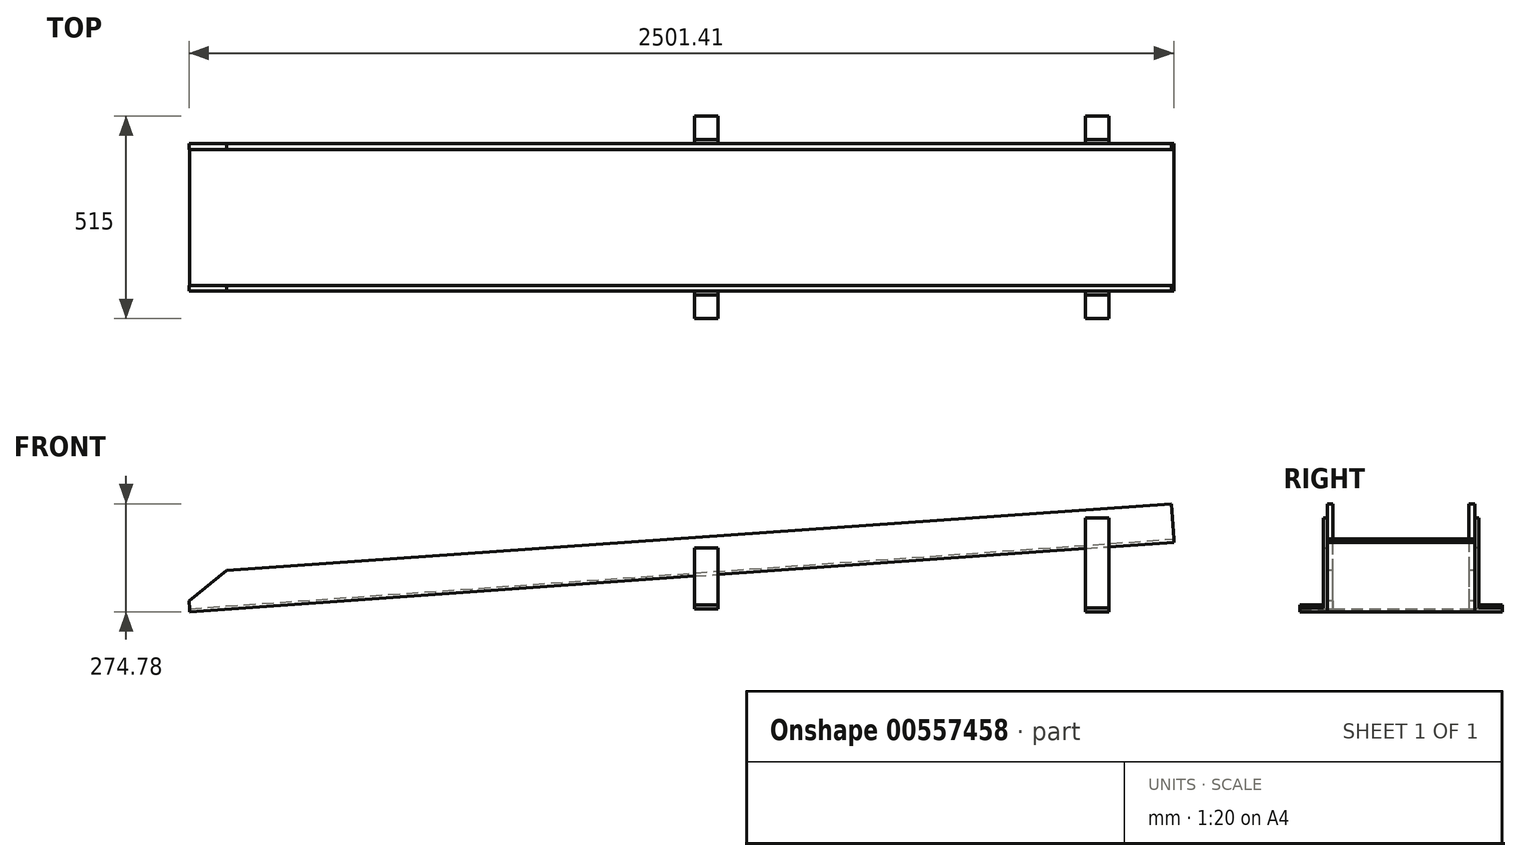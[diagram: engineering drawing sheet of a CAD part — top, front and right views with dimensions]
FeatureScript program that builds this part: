
annotation { "Feature Type Name" : "Feature", "Feature Type Description" : "" }
export const myFeature = defineFeature(function(context is Context, id is Id, definition is map)
    precondition{}
    {
        {
            var Q0;
            Q0=qCreatedBy(makeId("Front.planeOp"),FACE);
            var sketch = newSketch(context, id + "F0", { "sketchPlane" : qUnion([Q0])});
            skLineSegment(sketch, "E0", {"start": v(-1084.35, 0) * mm, "end": v(1415.65, 176.98) * mm});
            skLineSegment(sketch, "E1", {"start": v(1415.65, 176.98) * mm, "end": v(1415.65, 0) * mm});
            skLineSegment(sketch, "E2", {"start": v(1415.65, 0) * mm, "end": v(-1084.35, 0) * mm});
            skLineSegment(sketch, "E3", {"start": v(1415.65, 185) * mm, "end": v(-1084.35, 8.02) * mm});
            skLineSegment(sketch, "E4", {"start": v(-1084.35, 8.02) * mm, "end": v(-1084.35, 0) * mm});
            skLineSegment(sketch, "E5", {"start": v(1415.65, 176.98) * mm, "end": v(1415.65, 185) * mm});
            skSolve(sketch);
        }
        {
            var Q0;
            Q0=makeQuery(id+"F0.imprint","IMPRINT",FACE,{"disambiguationData":[TD([[makeQuery(id+"F0.imprint","IMPRINT",EDGE,{"derivedFrom":sQuery(id+"F0.wireOp",EDGE,"E0")}),1.0]])]});
            extrude(context, id + "F1", {"entities" : qUnion([Q0]), "endBound" : BoundingType.SYMMETRIC, "depth" : 375 * mm, "offsetDistance" : 25 * mm});
        }
        {
            var Q0;
            Q0=makeQuery(id+"F1.opExtrude","SWEPT_FACE",FACE,{"disambiguationData":[OSD([sQuery(id+"F0.wireOp",EDGE,"E3")])]});
            var sketch = newSketch(context, id + "F2", { "sketchPlane" : qUnion([Q0])});
            skLineSegment(sketch, "E6", {"start": v(1425.18, -187.5) * mm, "end": v(-1081.07, -187.5) * mm});
            skLineSegment(sketch, "E7", {"start": v(-1081.07, -187.5) * mm, "end": v(-1081.07, -172.5) * mm});
            skLineSegment(sketch, "E8", {"start": v(-1081.07, -172.5) * mm, "end": v(1425.18, -172.5) * mm});
            skLineSegment(sketch, "E9", {"start": v(1425.18, -172.5) * mm, "end": v(1425.18, -187.5) * mm});
            skLineSegment(sketch, "E10", {"start": v(1425.18, 187.5) * mm, "end": v(1425.18, 172.5) * mm});
            skLineSegment(sketch, "E11", {"start": v(1425.18, 172.5) * mm, "end": v(-1081.07, 172.5) * mm});
            skLineSegment(sketch, "E12", {"start": v(-1081.07, 172.5) * mm, "end": v(-1081.07, 187.5) * mm});
            skLineSegment(sketch, "E13", {"start": v(-1081.07, 187.5) * mm, "end": v(1425.18, 187.5) * mm});
            skSolve(sketch);
        }
        {
            var Q0;
            Q0 = qSketchRegion(id + "F2", true);
            extrude(context, id + "F3", {"entities" : qUnion([Q0]), "operationType" : NewBodyOperationType.ADD, "depth" : 90 * mm, "offsetDistance" : 25 * mm});
        }
        {
            var Q0;
            Q0=makeQuery(id+"F3.boolean.opBoolean","MERGE",FACE,{"derivedFrom":[makeQuery(id+"F1.opExtrude","CAP_FACE",FACE,{"disambiguationData":[OSD([sQuery(id+"F0.wireOp",EDGE,"E0"),sQuery(id+"F0.wireOp",EDGE,"E3"),sQuery(id+"F0.wireOp",EDGE,"E4"),sQuery(id+"F0.wireOp",EDGE,"E5")])],"isStart":false}),makeQuery(id+"F3.opExtrude","SWEPT_FACE",FACE,{"disambiguationData":[OSD([sQuery(id+"F2.wireOp",EDGE,"E6")])]})]});
            var sketch = newSketch(context, id + "F4", { "sketchPlane" : qUnion([Q0])});
            skLineSegment(sketch, "E14", {"start": v(1191.53, 238.96) * mm, "end": v(1191.53, 0) * mm});
            skLineSegment(sketch, "E15", {"start": v(1191.53, 0) * mm, "end": v(1251.53, 0) * mm});
            skLineSegment(sketch, "E16", {"start": v(1251.53, 0) * mm, "end": v(1251.53, 238.96) * mm});
            skLineSegment(sketch, "E17", {"start": v(1251.53, 238.96) * mm, "end": v(1191.53, 238.96) * mm});
            skLineSegment(sketch, "E18", {"start": v(1191.53, 10) * mm, "end": v(1251.53, 10) * mm});
            skLineSegment(sketch, "E19", {"start": v(198.02, 161.9) * mm, "end": v(198.02, 8.02) * mm});
            skLineSegment(sketch, "E20", {"start": v(198.02, 8.02) * mm, "end": v(258.02, 8.02) * mm});
            skLineSegment(sketch, "E21", {"start": v(258.02, 8.02) * mm, "end": v(258.02, 161.9) * mm});
            skLineSegment(sketch, "E22", {"start": v(258.02, 161.9) * mm, "end": v(198.02, 161.9) * mm});
            skLineSegment(sketch, "E23", {"start": v(198.02, 18.02) * mm, "end": v(258.02, 18.02) * mm});
            skSolve(sketch);
        }
        {
            var Q0;
            {var subQ0=sQuery(id+"F4.wireOp",EDGE,"E20");Q0=makeQuery(id+"F4.imprint","IMPRINT",FACE,{"disambiguationData":[TD([[makeQuery(id+"F4.imprint","IMPRINT",EDGE,{"derivedFrom":subQ0}),1.0]])]});}
            var Q1;
            {var subQ0=sQuery(id+"F4.wireOp",EDGE,"E15");Q1=makeQuery(id+"F4.imprint","IMPRINT",FACE,{"disambiguationData":[TD([[makeQuery(id+"F4.imprint","IMPRINT",EDGE,{"derivedFrom":subQ0}),1.0]])]});}
            extrude(context, id + "F5", {"entities" : qUnion([Q0, Q1]), "operationType" : NewBodyOperationType.ADD, "depth" : 70 * mm, "offsetDistance" : 25 * mm});
        }
        {
            var Q0;
            Q0 = qSketchRegion(id + "F4", true);
            extrude(context, id + "F6", {"entities" : qUnion([Q0]), "depth" : 10 * mm, "offsetDistance" : 25 * mm});
        }
        {
            var Q0;
            Q0=makeQuery(id+"F5.opExtrude","SWEPT_BODY",BODY,{"disambiguationData":[OSD([sQuery(id+"F4.wireOp",EDGE,"E19"),sQuery(id+"F4.wireOp",EDGE,"E20"),sQuery(id+"F4.wireOp",EDGE,"E21"),sQuery(id+"F4.wireOp",EDGE,"E23")])]});
            var Q1;
            Q1=makeQuery(id+"F6.opExtrude","SWEPT_BODY",BODY,{"disambiguationData":[OSD([sQuery(id+"F4.wireOp",EDGE,"E19"),sQuery(id+"F4.wireOp",EDGE,"E20"),sQuery(id+"F4.wireOp",EDGE,"E21"),sQuery(id+"F4.wireOp",EDGE,"E22")])]});
            var Q2;
            Q2=makeQuery(id+"F6.opExtrude","SWEPT_BODY",BODY,{"disambiguationData":[OSD([sQuery(id+"F4.wireOp",EDGE,"E14"),sQuery(id+"F4.wireOp",EDGE,"E15"),sQuery(id+"F4.wireOp",EDGE,"E16"),sQuery(id+"F4.wireOp",EDGE,"E17")])]});
            var Q3;
            Q3=makeQuery(id+"F5.opExtrude","SWEPT_BODY",BODY,{"disambiguationData":[OSD([sQuery(id+"F4.wireOp",EDGE,"E14"),sQuery(id+"F4.wireOp",EDGE,"E15"),sQuery(id+"F4.wireOp",EDGE,"E16"),sQuery(id+"F4.wireOp",EDGE,"E18")])]});
            var Q4;
            Q4=qCreatedBy(makeId("Front.planeOp"),FACE);
            mirror(context, id + "F7", {"operationType" : NewBodyOperationType.ADD, "entities" : qUnion([Q0, Q1, Q2, Q3]), "mirrorPlane" : qUnion([Q4])});
        }
        {
            var Q0;
            Q0=makeQuery(id+"F3.boolean.opBoolean","MERGE",FACE,{"derivedFrom":[makeQuery(id+"F1.opExtrude","CAP_FACE",FACE,{"disambiguationData":[OSD([sQuery(id+"F0.wireOp",EDGE,"E0"),sQuery(id+"F0.wireOp",EDGE,"E3"),sQuery(id+"F0.wireOp",EDGE,"E4"),sQuery(id+"F0.wireOp",EDGE,"E5")])],"isStart":false}),makeQuery(id+"F3.opExtrude","SWEPT_FACE",FACE,{"disambiguationData":[OSD([sQuery(id+"F2.wireOp",EDGE,"E6")])]})]});
            var sketch = newSketch(context, id + "F8", { "sketchPlane" : qUnion([Q0])});
            skLineSegment(sketch, "E24", {"start": v(-990.95, 104.86) * mm, "end": v(-1085.76, 27.97) * mm});
            skLineSegment(sketch, "E25", {"start": v(-1085.76, 27.97) * mm, "end": v(-1090.7, 97.8) * mm});
            skLineSegment(sketch, "E26", {"start": v(-1090.7, 97.8) * mm, "end": v(-990.95, 104.86) * mm});
            skSolve(sketch);
        }
        {
            var Q0;
            Q0 = qSketchRegion(id + "F8", true);
            var Q1;
            Q1=makeQuery(id+"F3.boolean.opBoolean","MERGE",FACE,{"derivedFrom":[makeQuery(id+"F1.opExtrude","CAP_FACE",FACE,{"disambiguationData":[OSD([sQuery(id+"F0.wireOp",EDGE,"E0"),sQuery(id+"F0.wireOp",EDGE,"E3"),sQuery(id+"F0.wireOp",EDGE,"E4"),sQuery(id+"F0.wireOp",EDGE,"E5")])],"isStart":true}),makeQuery(id+"F3.opExtrude","SWEPT_FACE",FACE,{"disambiguationData":[OSD([sQuery(id+"F2.wireOp",EDGE,"E13")])]})]});
            extrude(context, id + "F9", {"entities" : qUnion([Q0]), "operationType" : NewBodyOperationType.REMOVE, "endBound" : BoundingType.UP_TO_SURFACE, "oppositeDirection" : true, "depth" : 25 * mm, "endBoundEntityFace" : qUnion([Q1]), "offsetDistance" : 25 * mm});
        }
    });
